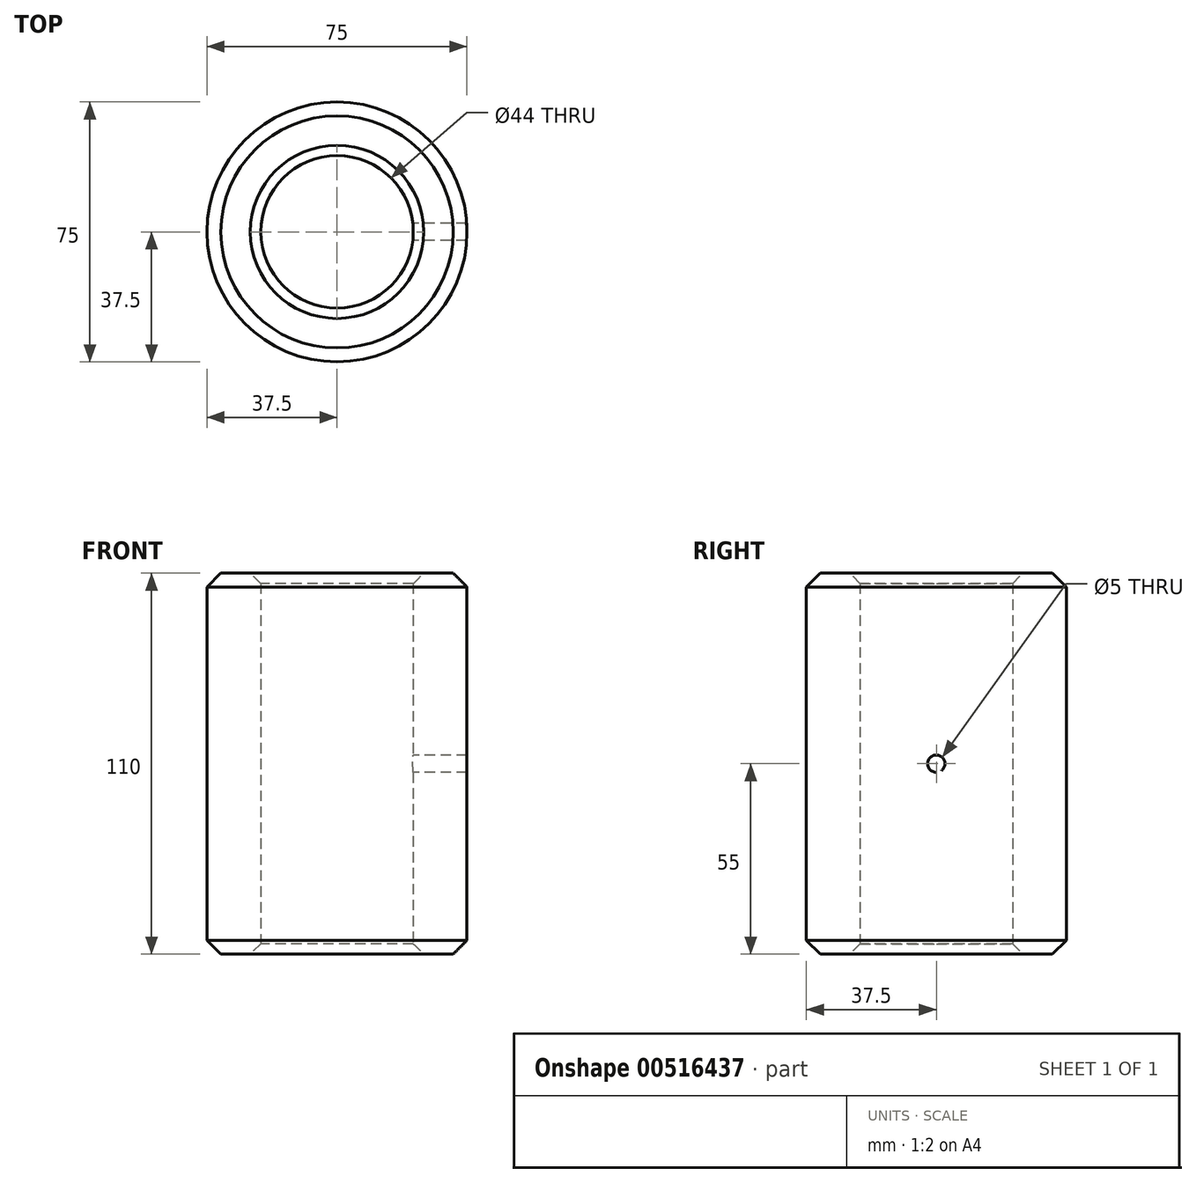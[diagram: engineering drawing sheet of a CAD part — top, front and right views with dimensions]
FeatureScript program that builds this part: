
annotation { "Feature Type Name" : "Feature", "Feature Type Description" : "" }
export const myFeature = defineFeature(function(context is Context, id is Id, definition is map)
    precondition{}
    {
        {
            var Q0;
            Q0=qCreatedBy(makeId("Top.planeOp"),FACE);
            var sketch = newSketch(context, id + "F0", { "sketchPlane" : qUnion([Q0])});
            skCircle(sketch, "E0", {"center": v(0, 0) * mm, "radius": 37.5 * mm});
            skCircle(sketch, "E1", {"center": v(0, 0) * mm, "radius": 22 * mm});
            skSolve(sketch);
        }
        {
            var Q0;
            Q0 = qSketchRegion(id + "F0", true);
            extrude(context, id + "F1", {"entities" : qUnion([Q0]), "depth" : 110 * mm, "offsetDistance" : 25 * mm});
        }
        {
            var Q0;
            Q0=makeQuery(id+"F1.opExtrude","CAP_EDGE",EDGE,{"disambiguationData":[OSD([sQuery(id+"F0.wireOp",EDGE,"E0")])],"isStart":false});
            var Q1;
            Q1=makeQuery(id+"F1.opExtrude","CAP_EDGE",EDGE,{"disambiguationData":[OSD([sQuery(id+"F0.wireOp",EDGE,"E0")])],"isStart":true});
            chamfer(context, id + "F2", {"entities" : qUnion([Q0, Q1]), "width" : 4 * mm, "tangentPropagation" : true});
        }
        {
            var Q0;
            Q0=makeQuery(id+"F1.opExtrude","CAP_EDGE",EDGE,{"disambiguationData":[OSD([sQuery(id+"F0.wireOp",EDGE,"E1")])],"isStart":false});
            var Q1;
            Q1=makeQuery(id+"F1.opExtrude","CAP_EDGE",EDGE,{"disambiguationData":[OSD([sQuery(id+"F0.wireOp",EDGE,"E1")])],"isStart":true});
            chamfer(context, id + "F3", {"entities" : qUnion([Q0, Q1]), "width" : 3 * mm, "tangentPropagation" : true});
        }
        {
            var Q0;
            Q0=qCreatedBy(makeId("Right.planeOp"),FACE);
            var sketch = newSketch(context, id + "F4", { "sketchPlane" : qUnion([Q0])});
            skCircle(sketch, "E2", {"center": v(0, 55) * mm, "radius": 2.5 * mm});
            skSolve(sketch);
        }
        {
            var Q0;
            Q0 = qSketchRegion(id + "F4", true);
            var Q1;
            Q1=makeQuery(id+"F1.opExtrude","SWEPT_FACE",FACE,{"disambiguationData":[OSD([sQuery(id+"F0.wireOp",EDGE,"E0")])]});
            extrude(context, id + "F5", {"entities" : qUnion([Q0]), "operationType" : NewBodyOperationType.REMOVE, "endBound" : BoundingType.UP_TO_SURFACE, "depth" : 75 * mm, "endBoundEntityFace" : qUnion([Q1]), "offsetDistance" : 25 * mm});
        }
    });
